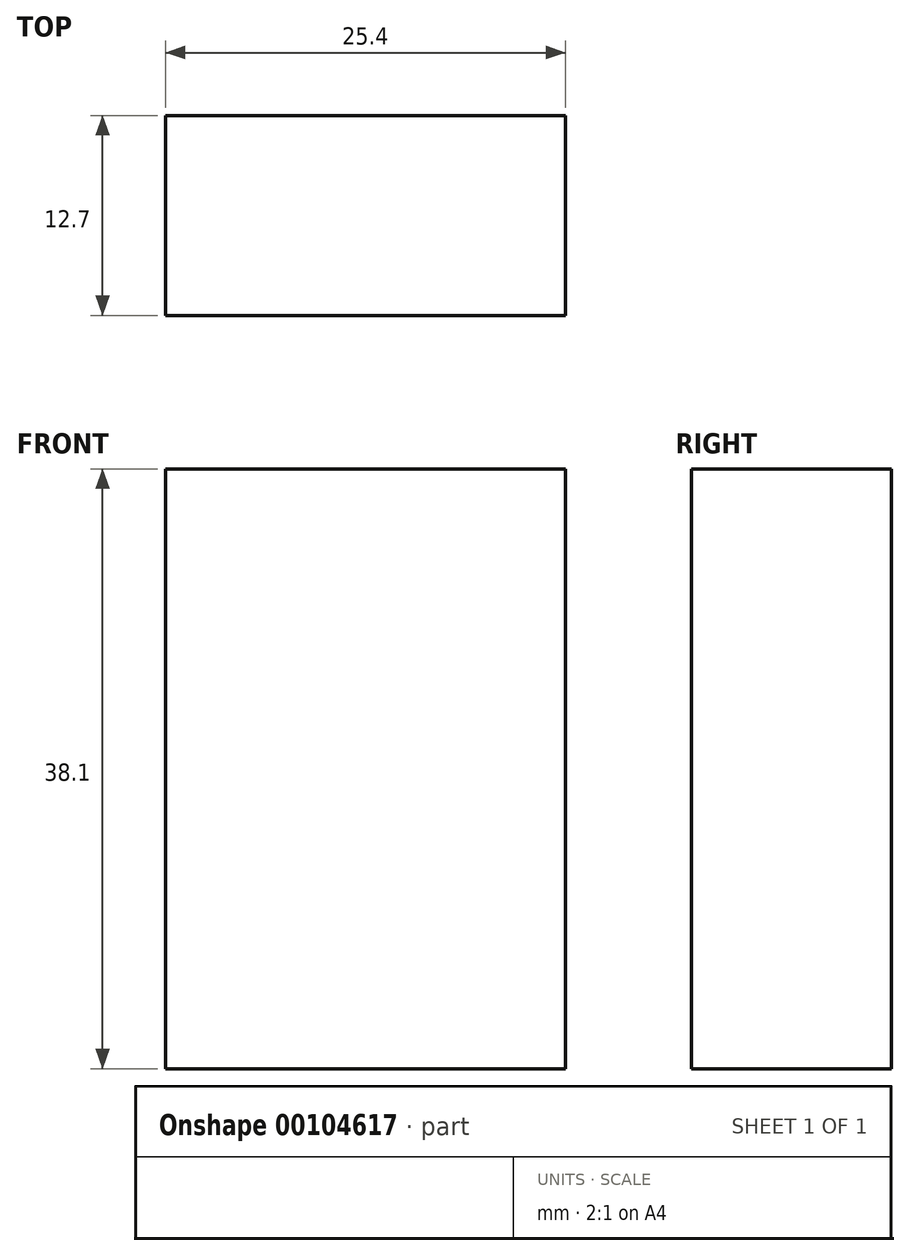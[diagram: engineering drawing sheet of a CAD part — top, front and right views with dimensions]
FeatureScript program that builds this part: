
annotation { "Feature Type Name" : "Feature", "Feature Type Description" : "" }
export const myFeature = defineFeature(function(context is Context, id is Id, definition is map)
    precondition{}
    {
        {
            var Q0;
            Q0=qCreatedBy(makeId("Top.planeOp"),FACE);
            var sketch = newSketch(context, id + "F0", { "sketchPlane" : qUnion([Q0])});
            skLineSegment(sketch, "E0.bottom", {"start": v(-12.7, -6.35) * mm, "end": v(12.7, -6.35) * mm});
            skLineSegment(sketch, "E0.top", {"start": v(-12.7, 6.35) * mm, "end": v(12.7, 6.35) * mm});
            skLineSegment(sketch, "E0.left", {"start": v(-12.7, -6.35) * mm, "end": v(-12.7, 6.35) * mm});
            skLineSegment(sketch, "E0.right", {"start": v(12.7, -6.35) * mm, "end": v(12.7, 6.35) * mm});
            skPoint(sketch, "E0.middle", {"position": v(0, 0) * mm});
            skSolve(sketch);
        }
        {
            var Q0;
            Q0=makeQuery(id+"F0.imprint","IMPRINT",FACE,{"disambiguationData":[TD([[makeQuery(id+"F0.imprint","IMPRINT",EDGE,{"derivedFrom":sQuery(id+"F0.wireOp",EDGE,"E0.bottom")}),1.0]])]});
            extrude(context, id + "F1", {"entities" : qUnion([Q0]), "depth" : 38.1 * mm});
        }
    });
